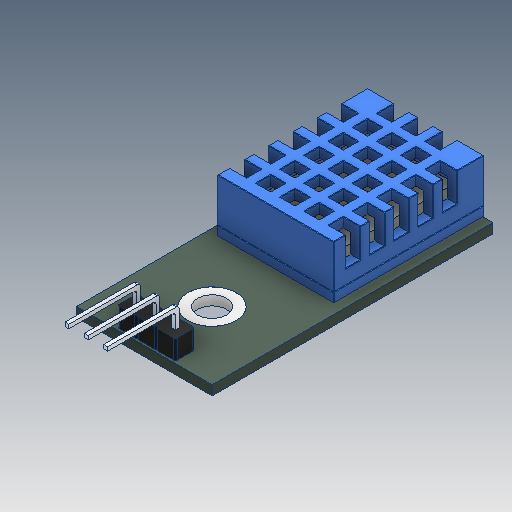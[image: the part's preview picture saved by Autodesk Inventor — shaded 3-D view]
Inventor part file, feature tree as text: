
AUTODESK INVENTOR PART (.ipt)
format: ipt  version: 2018 (Build 220112000, 112)  size: 439,808 bytes
history: native  units: mm
features: fillet x1, other x1
ambient origin geometry x8: Origin, YZ Plane, XZ Plane, XY Plane, X Axis, Y Axis, Z Axis, Center Point
bodies: Volumenkörper1 (feature_tree), Volumenkörper2 (feature_tree)
feature tree (2):
  fillet  "Fillet1"  [1 undecoded]
  other  "Cut-Extrude6"
note: 1 required parameter value undecoded (feature->parameter linkage not recoverable at this tier; creation-order binding heuristic only, values carry confidence <= 0.55)
